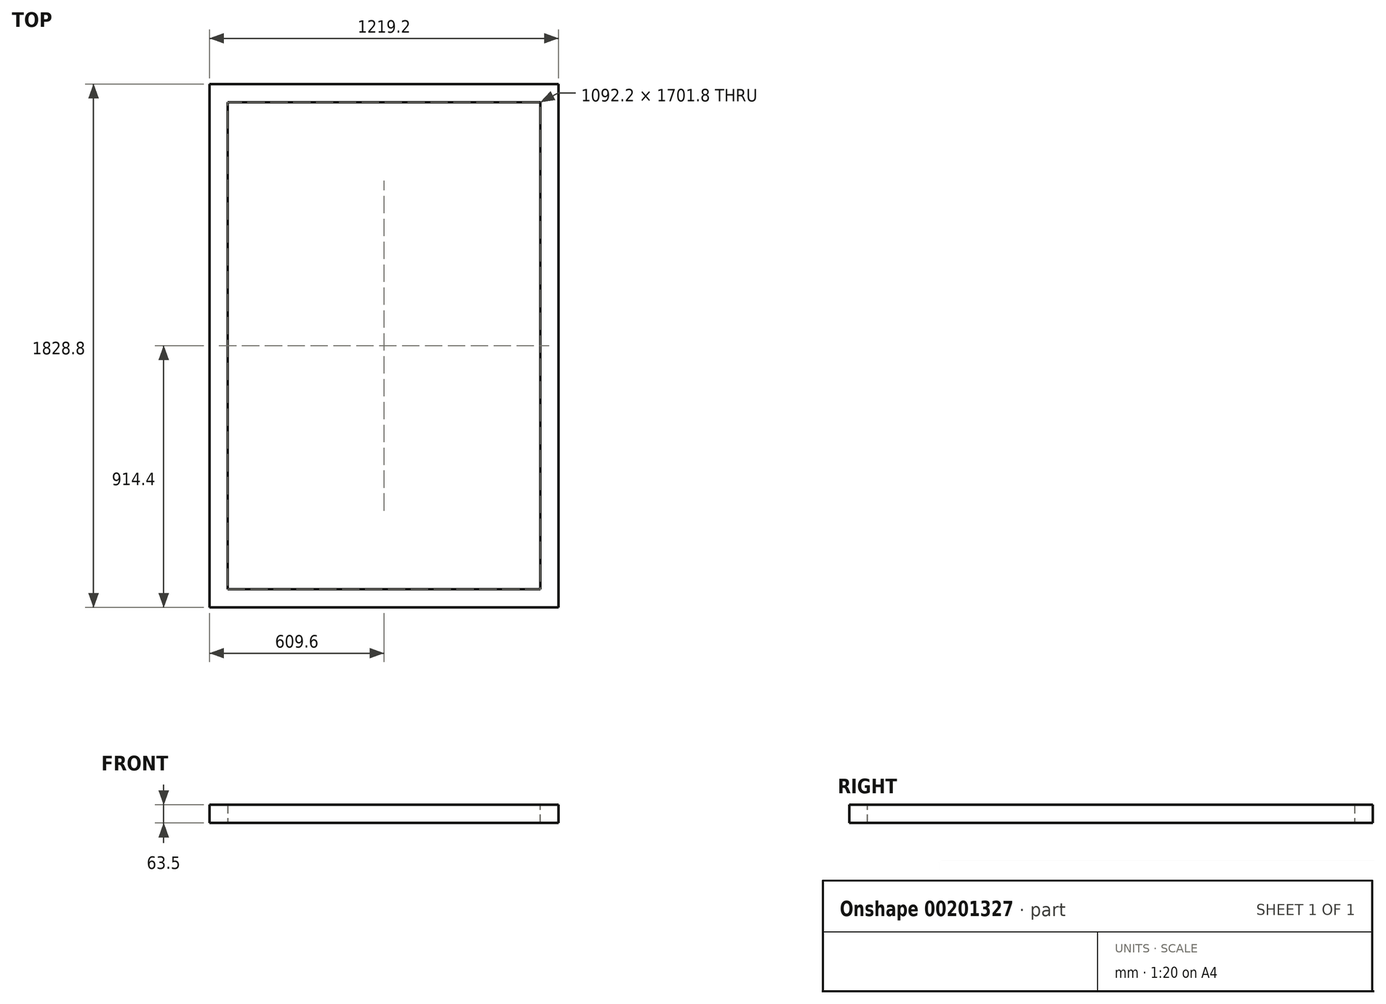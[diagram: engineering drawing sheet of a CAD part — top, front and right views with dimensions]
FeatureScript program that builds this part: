
annotation { "Feature Type Name" : "Feature", "Feature Type Description" : "" }
export const myFeature = defineFeature(function(context is Context, id is Id, definition is map)
    precondition{}
    {
        {
            var Q0;
            Q0=qCreatedBy(makeId("Front.planeOp"),FACE);
            var sketch = newSketch(context, id + "F0", { "sketchPlane" : qUnion([Q0])});
            skLineSegment(sketch, "E0.bottom", {"start": v(0, 0) * mm, "end": v(63.5, 0) * mm});
            skLineSegment(sketch, "E0.top", {"start": v(0, 63.5) * mm, "end": v(63.5, 63.5) * mm});
            skLineSegment(sketch, "E0.left", {"start": v(0, 0) * mm, "end": v(0, 63.5) * mm});
            skLineSegment(sketch, "E0.right", {"start": v(63.5, 0) * mm, "end": v(63.5, 63.5) * mm});
            skSolve(sketch);
        }
        {
            var Q0;
            Q0=makeQuery(id+"F0.imprint","IMPRINT",FACE,{"disambiguationData":[TD([[makeQuery(id+"F0.imprint","IMPRINT",EDGE,{"derivedFrom":sQuery(id+"F0.wireOp",EDGE,"E0.bottom")}),1.0]])]});
            extrude(context, id + "F1", {"entities" : qUnion([Q0]), "oppositeDirection" : true, "depth" : 1828.8 * mm});
        }
        {
            var Q0;
            Q0=makeQuery(id+"F1.opExtrude","SWEPT_FACE",FACE,{"disambiguationData":[OSD([sQuery(id+"F0.wireOp",EDGE,"E0.right")])]});
            var sketch = newSketch(context, id + "F2", { "sketchPlane" : qUnion([Q0])});
            skLineSegment(sketch, "E1.bottom", {"start": v(0, 0) * mm, "end": v(63.5, 0) * mm});
            skLineSegment(sketch, "E1.top", {"start": v(0, 63.5) * mm, "end": v(63.5, 63.5) * mm});
            skLineSegment(sketch, "E1.left", {"start": v(0, 0) * mm, "end": v(0, 63.5) * mm});
            skLineSegment(sketch, "E1.right", {"start": v(63.5, 0) * mm, "end": v(63.5, 63.5) * mm});
            skSolve(sketch);
        }
        {
            var Q0;
            Q0=makeQuery(id+"F2.imprint","IMPRINT",FACE,{"disambiguationData":[TD([[makeQuery(id+"F2.imprint","IMPRINT",EDGE,{"derivedFrom":sQuery(id+"F2.wireOp",EDGE,"E1.bottom")}),-1.0]])]});
            extrude(context, id + "F3", {"entities" : qUnion([Q0]), "operationType" : NewBodyOperationType.ADD, "depth" : 1092.2 * mm});
        }
        {
            var Q0;
            Q0=makeQuery(id+"F3.boolean.opBoolean","MERGE",FACE,{"derivedFrom":[makeQuery(id+"F1.opExtrude","CAP_FACE",FACE,{"disambiguationData":[OSD([sQuery(id+"F0.wireOp",EDGE,"E0.bottom"),sQuery(id+"F0.wireOp",EDGE,"E0.top"),sQuery(id+"F0.wireOp",EDGE,"E0.left"),sQuery(id+"F0.wireOp",EDGE,"E0.right")])],"isStart":true}),makeQuery(id+"F3.opExtrude","SWEPT_FACE",FACE,{"disambiguationData":[OSD([sQuery(id+"F2.wireOp",EDGE,"E1.left")])]})]});
            var sketch = newSketch(context, id + "F4", { "sketchPlane" : qUnion([Q0])});
            skLineSegment(sketch, "E2.bottom", {"start": v(1155.7, 0) * mm, "end": v(1219.2, 0) * mm});
            skLineSegment(sketch, "E2.top", {"start": v(1155.7, 63.5) * mm, "end": v(1219.2, 63.5) * mm});
            skLineSegment(sketch, "E2.left", {"start": v(1155.7, 0) * mm, "end": v(1155.7, 63.5) * mm});
            skLineSegment(sketch, "E2.right", {"start": v(1219.2, 0) * mm, "end": v(1219.2, 63.5) * mm});
            skSolve(sketch);
        }
        {
            var Q0;
            Q0=makeQuery(id+"F4.imprint","IMPRINT",FACE,{"disambiguationData":[TD([[makeQuery(id+"F4.imprint","IMPRINT",EDGE,{"derivedFrom":sQuery(id+"F4.wireOp",EDGE,"E2.bottom")}),1.0]])]});
            extrude(context, id + "F5", {"entities" : qUnion([Q0]), "operationType" : NewBodyOperationType.ADD, "oppositeDirection" : true, "depth" : 1828.8 * mm});
        }
        {
            var Q0;
            Q0=makeQuery(id+"F1.opExtrude","SWEPT_FACE",FACE,{"disambiguationData":[OSD([sQuery(id+"F0.wireOp",EDGE,"E0.right")])]});
            var sketch = newSketch(context, id + "F6", { "sketchPlane" : qUnion([Q0])});
            skLineSegment(sketch, "E3.bottom", {"start": v(1828.8, 63.5) * mm, "end": v(1765.3, 63.5) * mm});
            skLineSegment(sketch, "E3.top", {"start": v(1828.8, 0) * mm, "end": v(1765.3, 0) * mm});
            skLineSegment(sketch, "E3.left", {"start": v(1828.8, 63.5) * mm, "end": v(1828.8, 0) * mm});
            skLineSegment(sketch, "E3.right", {"start": v(1765.3, 63.5) * mm, "end": v(1765.3, 0) * mm});
            skSolve(sketch);
        }
        {
            var Q0;
            Q0=makeQuery(id+"F6.imprint","IMPRINT",FACE,{"disambiguationData":[TD([[makeQuery(id+"F6.imprint","IMPRINT",EDGE,{"derivedFrom":sQuery(id+"F6.wireOp",EDGE,"E3.bottom")}),1.0]])]});
            extrude(context, id + "F7", {"entities" : qUnion([Q0]), "operationType" : NewBodyOperationType.ADD, "depth" : 1092.2 * mm});
        }
    });
